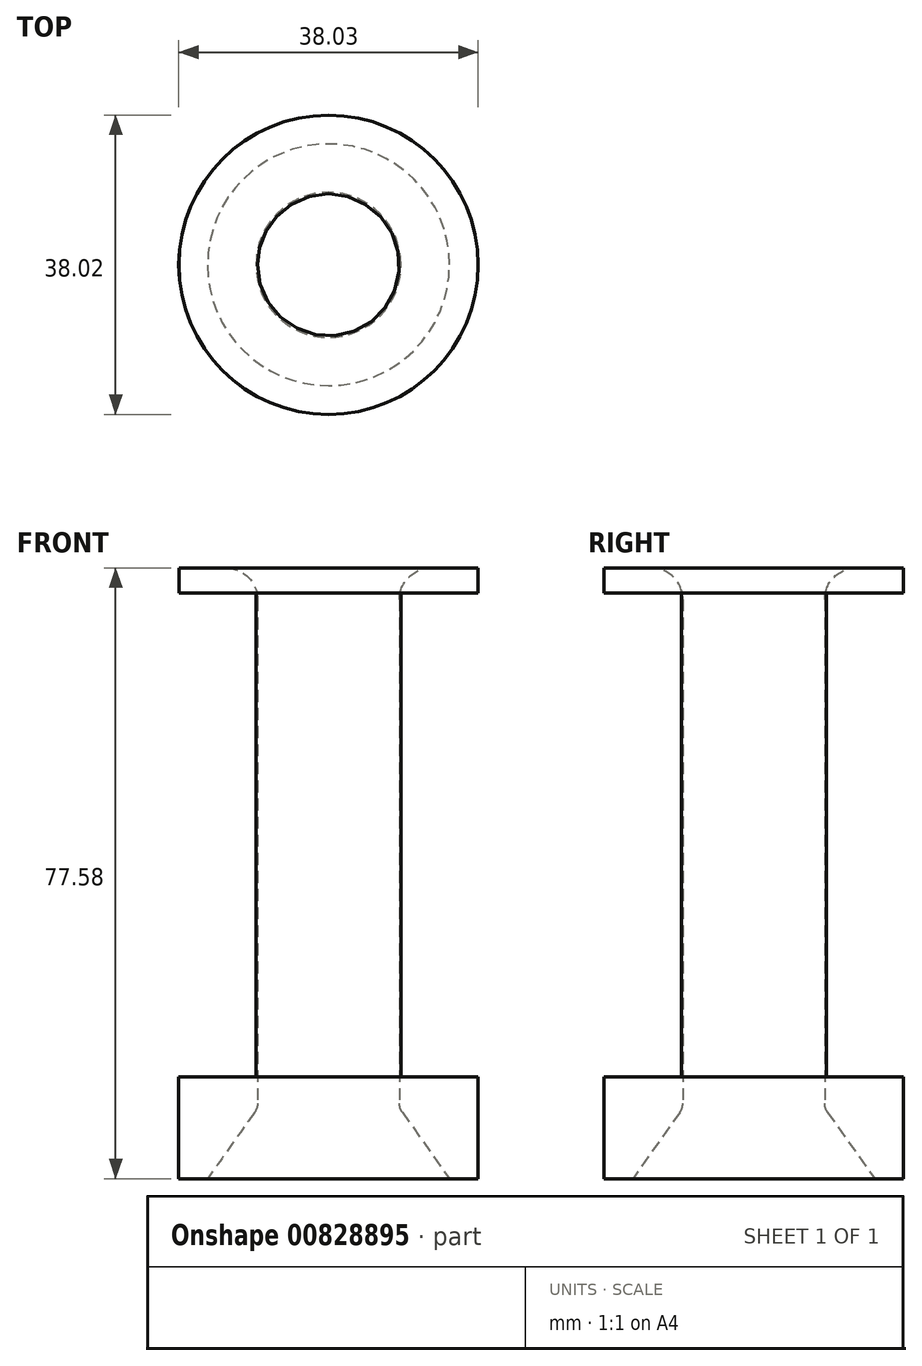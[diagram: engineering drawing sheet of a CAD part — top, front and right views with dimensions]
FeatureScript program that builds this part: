
annotation { "Feature Type Name" : "Feature", "Feature Type Description" : "" }
export const myFeature = defineFeature(function(context is Context, id is Id, definition is map)
    precondition{}
    {
        {
            var Q0;
            Q0=qCreatedBy(makeId("Front.planeOp"),FACE);
            var sketch = newSketch(context, id + "F0", { "sketchPlane" : qUnion([Q0])});
            skLineSegment(sketch, "E0.bottom", {"start": v(-9.01, 32.06) * mm, "end": v(8.99, 32.06) * mm});
            skLineSegment(sketch, "E0.top", {"start": v(-9.01, 102.06) * mm, "end": v(8.99, 102.06) * mm});
            skLineSegment(sketch, "E0.left", {"start": v(-9.01, 32.06) * mm, "end": v(-9.01, 102.06) * mm});
            skLineSegment(sketch, "E0.right", {"start": v(8.99, 32.06) * mm, "end": v(8.99, 102.06) * mm});
            skLineSegment(sketch, "E1", {"start": v(-9.01, 102.06) * mm, "end": v(8.99, 102.06) * mm, "construction": true});
            skLineSegment(sketch, "E2", {"start": v(-9.01, 32.06) * mm, "end": v(-0.01, 32.06) * mm, "construction": true});
            skLineSegment(sketch, "E3", {"start": v(-0.01, 32.06) * mm, "end": v(-0.01, 287.98) * mm, "construction": true});
            skSolve(sketch);
        }
        {
            var Q0;
            Q0=qCreatedBy(makeId("Front.planeOp"),FACE);
            var sketch = newSketch(context, id + "F1", { "sketchPlane" : qUnion([Q0])});
            skLineSegment(sketch, "E4", {"start": v(-9.03, 33.43) * mm, "end": v(-9.03, 102.06) * mm});
            skLineSegment(sketch, "E5", {"start": v(-9.03, 102.06) * mm, "end": v(-19.03, 102.06) * mm});
            skLineSegment(sketch, "E6", {"start": v(-19.03, 102.06) * mm, "end": v(-19.03, 98.88) * mm});
            skLineSegment(sketch, "E7", {"start": v(-9.93, -19906.31) * mm, "end": v(-19.93, -19906.3) * mm});
            skLineSegment(sketch, "E8", {"start": v(-19.93, -19906.3) * mm, "end": v(-19.93, -19908.25) * mm});
            skLineSegment(sketch, "E9", {"start": v(-19.93, -19908.25) * mm, "end": v(-9.93, -19908.25) * mm});
            skPoint(sketch, "E10.end.orphan", {"position": v(0, 103.5) * mm});
            skLineSegment(sketch, "E11", {"start": v(-19.03, 37.43) * mm, "end": v(-9.23, 37.43) * mm});
            skLineSegment(sketch, "E12", {"start": v(-9.23, 37.43) * mm, "end": v(-9.23, 98.88) * mm});
            skLineSegment(sketch, "E13", {"start": v(-9.23, 98.88) * mm, "end": v(-19.03, 98.88) * mm});
            skLineSegment(sketch, "E14", {"start": v(-9.03, 110.25) * mm, "end": v(8.97, 110.25) * mm, "construction": true});
            skLineSegment(sketch, "E15", {"start": v(-9.03, 33.43) * mm, "end": v(-15.37, 24.48) * mm});
            skLineSegment(sketch, "E16", {"start": v(-15.37, 24.48) * mm, "end": v(-19.03, 24.48) * mm});
            skLineSegment(sketch, "E17", {"start": v(-19.03, 24.48) * mm, "end": v(-19.03, 37.43) * mm});
            skSolve(sketch);
        }
        {
            var Q0;
            Q0=makeQuery(id+"F1.imprint","IMPRINT",FACE,{"disambiguationData":[TD([[makeQuery(id+"F1.imprint","IMPRINT",EDGE,{"derivedFrom":sQuery(id+"F1.wireOp",EDGE,"E4")}),1.0]])]});
            var Q1;
            Q1=sQuery(id+"F0.wireOp",EDGE,"E3");
            revolve(context, id + "F2", {"surfaceOperationType" : NewSurfaceOperationType.NEW, "entities" : qUnion([Q0]), "axis" : qUnion([Q1]), "revolveType" : RevolveType.FULL});
        }
        {
            var Q0;
            Q0=makeQuery(id+"F2.opRevolve","SWEPT_EDGE",EDGE,{"disambiguationData":[OSD([sQuery(id+"F1.wireOp",EDGE,"E4"),sQuery(id+"F1.wireOp",EDGE,"E5")])]});
            fillet(context, id + "F3", {"entities" : qUnion([Q0]), "radius" : 4 * mm, "tangentPropagation" : true, "allowEdgeOverflow" : false});
        }
        {
            var Q0;
            Q0=makeQuery(id+"F2.opRevolve","SWEPT_EDGE",EDGE,{"disambiguationData":[OSD([sQuery(id+"F1.wireOp",EDGE,"E4"),sQuery(id+"F1.wireOp",EDGE,"E15")])]});
            fillet(context, id + "F4", {"entities" : qUnion([Q0]), "radius" : 2 * mm, "tangentPropagation" : true, "allowEdgeOverflow" : false});
        }
    });
